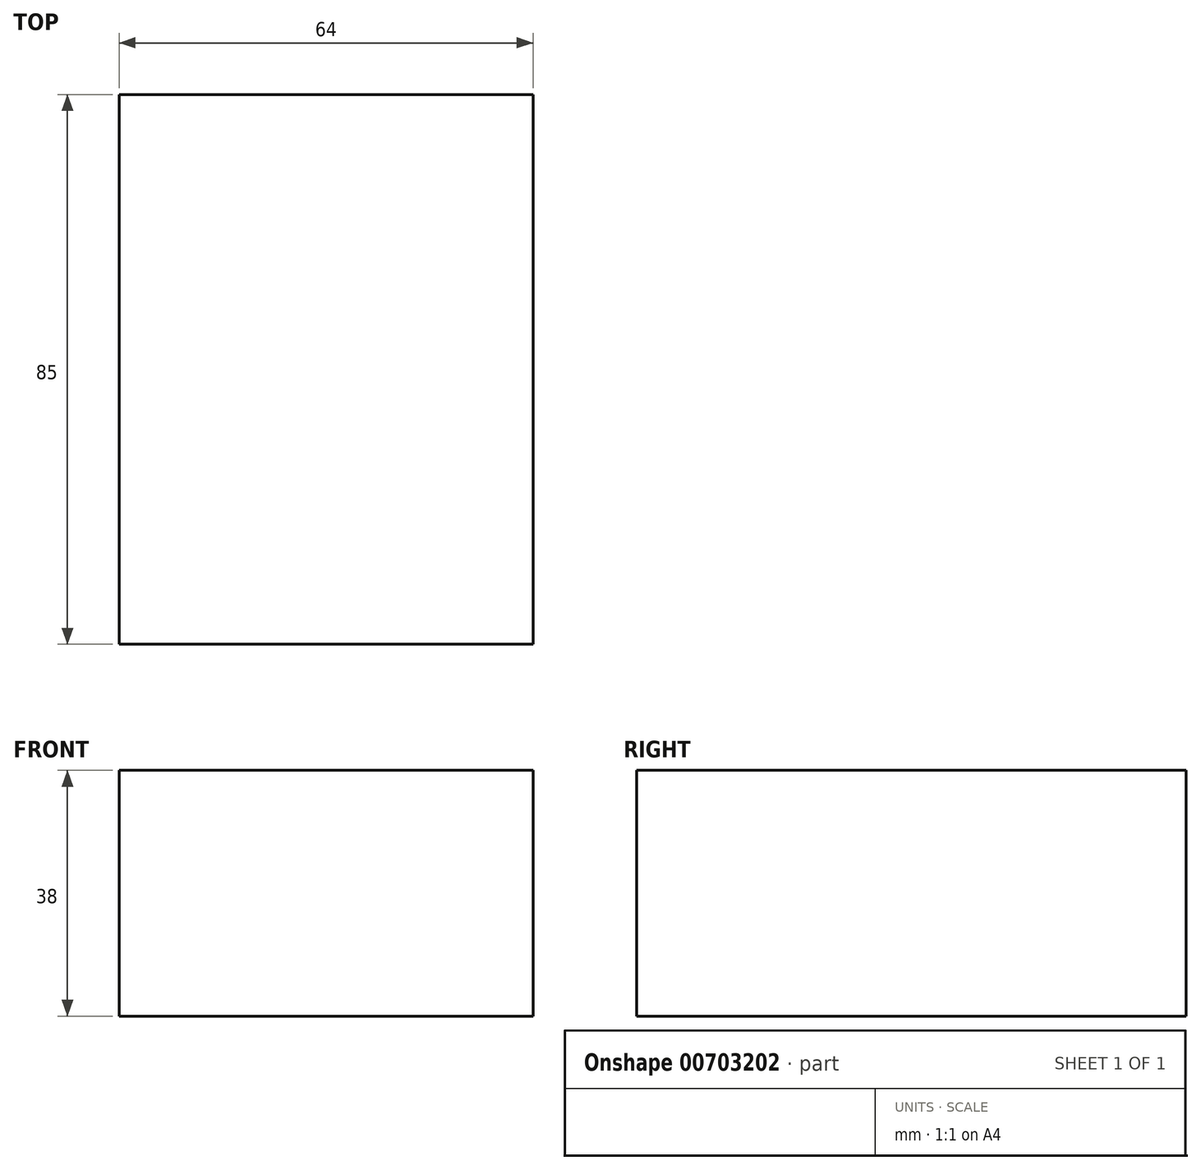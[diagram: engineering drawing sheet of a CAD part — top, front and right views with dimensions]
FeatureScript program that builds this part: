
annotation { "Feature Type Name" : "Feature", "Feature Type Description" : "" }
export const myFeature = defineFeature(function(context is Context, id is Id, definition is map)
    precondition{}
    {
        {
            var Q0;
            Q0=qCreatedBy(makeId("Top.planeOp"),FACE);
            var sketch = newSketch(context, id + "F0", { "sketchPlane" : qUnion([Q0])});
            skLineSegment(sketch, "E0.bottom", {"start": v(-32, 42.5) * mm, "end": v(32, 42.5) * mm});
            skLineSegment(sketch, "E0.top", {"start": v(-32, -42.5) * mm, "end": v(32, -42.5) * mm});
            skLineSegment(sketch, "E0.left", {"start": v(-32, 42.5) * mm, "end": v(-32, -42.5) * mm});
            skLineSegment(sketch, "E0.right", {"start": v(32, 42.5) * mm, "end": v(32, -42.5) * mm});
            skPoint(sketch, "E0.middle", {"position": v(0, 0) * mm});
            skSolve(sketch);
        }
        {
            var Q0;
            Q0=makeQuery(id+"F0.imprint","IMPRINT",FACE,{"disambiguationData":[TD([[makeQuery(id+"F0.imprint","IMPRINT",EDGE,{"derivedFrom":sQuery(id+"F0.wireOp",EDGE,"E0.bottom")}),-1.0]])]});
            extrude(context, id + "F1", {"entities" : qUnion([Q0]), "depth" : 38 * mm, "offsetDistance" : 25.4 * mm});
        }
    });
